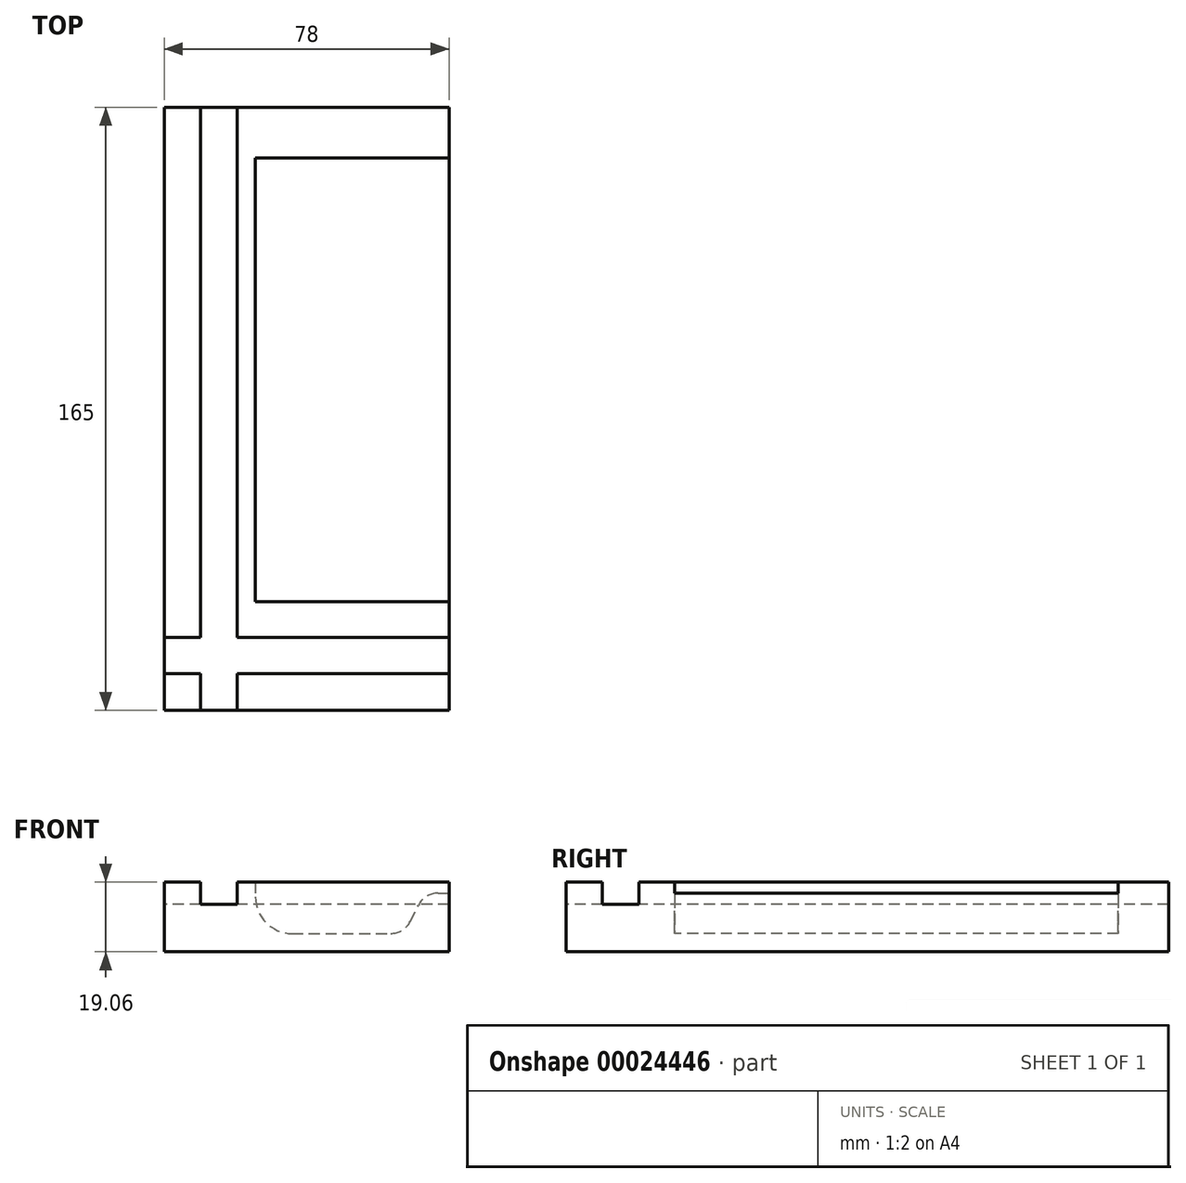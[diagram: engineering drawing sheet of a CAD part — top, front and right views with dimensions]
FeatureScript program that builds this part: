
annotation { "Feature Type Name" : "Feature", "Feature Type Description" : "" }
export const myFeature = defineFeature(function(context is Context, id is Id, definition is map)
    precondition{}
    {
        {
            var Q0;
            Q0=qCreatedBy(makeId("Front.planeOp"),FACE);
            var sketch = newSketch(context, id + "F0", { "sketchPlane" : qUnion([Q0])});
            skLineSegment(sketch, "E0.bottom", {"start": v(-39, 9.52) * mm, "end": v(39, 9.52) * mm});
            skLineSegment(sketch, "E0.top", {"start": v(-39, -9.52) * mm, "end": v(39, -9.52) * mm});
            skLineSegment(sketch, "E0.left", {"start": v(-39, 9.52) * mm, "end": v(-39, -9.52) * mm});
            skLineSegment(sketch, "E0.right", {"start": v(39, 9.52) * mm, "end": v(39, -9.52) * mm});
            skLineSegment(sketch, "E1", {"start": v(39, 9.52) * mm, "end": v(-39, -9.52) * mm, "construction": true});
            skSolve(sketch);
        }
        {
            var Q0;
            Q0=makeQuery(id+"F0.imprint","IMPRINT",FACE,{"disambiguationData":[TD([[makeQuery(id+"F0.imprint","IMPRINT",EDGE,{"derivedFrom":sQuery(id+"F0.wireOp",EDGE,"E0.bottom")}),-1.0]])]});
            extrude(context, id + "F1", {"entities" : qUnion([Q0]), "endBound" : BoundingType.SYMMETRIC, "depth" : 165 * mm});
        }
        {
            var Q0;
            Q0=qCreatedBy(makeId("Front.planeOp"),FACE);
            var sketch = newSketch(context, id + "F2", { "sketchPlane" : qUnion([Q0])});
            skLineSegment(sketch, "E2", {"start": v(-29, 9.52) * mm, "end": v(-29, 3.52) * mm});
            skLineSegment(sketch, "E3", {"start": v(-29, 3.52) * mm, "end": v(-19, 3.52) * mm});
            skLineSegment(sketch, "E4", {"start": v(-19, 3.52) * mm, "end": v(-19, 9.52) * mm});
            skLineSegment(sketch, "E5", {"start": v(-29, 9.52) * mm, "end": v(-19, 9.52) * mm});
            skSolve(sketch);
        }
        {
            var Q0;
            Q0 = qSketchRegion(id + "F2", true);
            extrude(context, id + "F3", {"entities" : qUnion([Q0]), "operationType" : NewBodyOperationType.REMOVE, "endBound" : BoundingType.SYMMETRIC, "oppositeDirection" : true, "depth" : 170 * mm});
        }
        {
            var Q0;
            Q0=qCreatedBy(makeId("Right.planeOp"),FACE);
            var sketch = newSketch(context, id + "F4", { "sketchPlane" : qUnion([Q0])});
            skLineSegment(sketch, "E6", {"start": v(-72.5, 9.52) * mm, "end": v(-72.5, 3.52) * mm});
            skLineSegment(sketch, "E7", {"start": v(-72.5, 3.52) * mm, "end": v(-62.5, 3.52) * mm});
            skLineSegment(sketch, "E8", {"start": v(-62.5, 3.52) * mm, "end": v(-62.5, 9.52) * mm});
            skLineSegment(sketch, "E9", {"start": v(-72.5, 9.52) * mm, "end": v(-62.5, 9.52) * mm});
            skSolve(sketch);
        }
        {
            var Q0;
            Q0 = qSketchRegion(id + "F4", true);
            extrude(context, id + "F5", {"entities" : qUnion([Q0]), "operationType" : NewBodyOperationType.REMOVE, "endBound" : BoundingType.SYMMETRIC, "depth" : 85 * mm});
        }
        {
            var Q0;
            Q0=qCreatedBy(makeId("Front.planeOp"),FACE);
            var sketch = newSketch(context, id + "F6", { "sketchPlane" : qUnion([Q0])});
            skLineSegment(sketch, "E10", {"start": v(-14, 9.52) * mm, "end": v(-14, 5.48) * mm});
            skLineSegment(sketch, "E11", {"start": v(-4, -4.52) * mm, "end": v(23.02, -4.52) * mm});
            skPoint(sketch, "E12.visualSharp", {"position": v(-14, -4.52) * mm});
            skArc(sketch, "E12.filletArc", {"start": v(-14, 5.47) * mm, "mid": v(-11.07, -1.6) * mm, "end": v(-4, -4.52) * mm});
            skLineSegment(sketch, "E13", {"start": v(28.36, -1.25) * mm, "end": v(30.65, 3.25) * mm});
            skLineSegment(sketch, "E14", {"start": v(36, 6.52) * mm, "end": v(39, 6.52) * mm});
            skPoint(sketch, "E15.visualSharp", {"position": v(32.32, 6.52) * mm});
            skArc(sketch, "E15.filletArc", {"start": v(36, 6.52) * mm, "mid": v(32.87, 5.64) * mm, "end": v(30.65, 3.25) * mm});
            skPoint(sketch, "E16.visualSharp", {"position": v(26.7, -4.52) * mm});
            skArc(sketch, "E16.filletArc", {"start": v(23.02, -4.52) * mm, "mid": v(26.15, -3.64) * mm, "end": v(28.36, -1.25) * mm});
            skLineSegment(sketch, "E17", {"start": v(-14, 9.52) * mm, "end": v(39, 9.53) * mm});
            skLineSegment(sketch, "E18", {"start": v(39, 9.53) * mm, "end": v(39, 6.52) * mm});
            skSolve(sketch);
        }
        {
            var Q0;
            Q0 = qSketchRegion(id + "F6", true);
            extrude(context, id + "F7", {"entities" : qUnion([Q0]), "operationType" : NewBodyOperationType.REMOVE, "oppositeDirection" : true, "depth" : 68.7 * mm, "offsetDistance" : 25 * mm, "hasSecondDirection" : true, "secondDirectionOppositeDirection" : false, "secondDirectionDepth" : 52.8 * mm});
        }
    });
